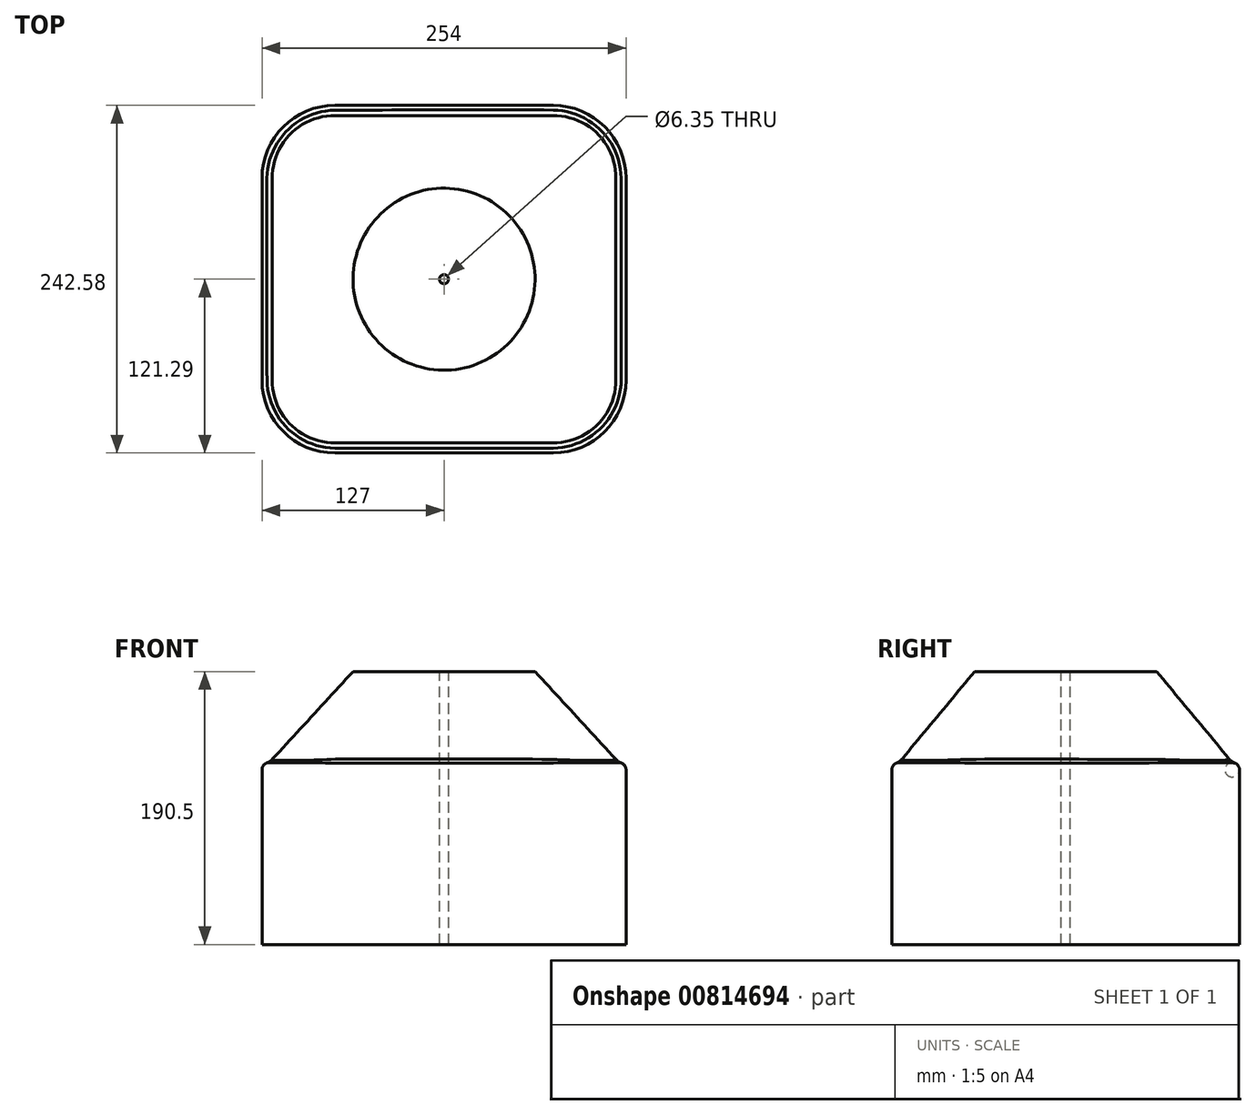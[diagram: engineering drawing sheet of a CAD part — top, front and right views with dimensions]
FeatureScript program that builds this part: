
annotation { "Feature Type Name" : "Feature", "Feature Type Description" : "" }
export const myFeature = defineFeature(function(context is Context, id is Id, definition is map)
    precondition{}
    {
        {
            var Q0;
            Q0=qCreatedBy(makeId("Front.planeOp"),FACE);
            var sketch = newSketch(context, id + "F0", { "sketchPlane" : qUnion([Q0])});
            skLineSegment(sketch, "E0.bottom", {"start": v(-127, 63.5) * mm, "end": v(127, 63.5) * mm});
            skLineSegment(sketch, "E0.top", {"start": v(-127, -63.5) * mm, "end": v(127, -63.5) * mm});
            skLineSegment(sketch, "E0.left", {"start": v(-127, 63.5) * mm, "end": v(-127, -63.5) * mm});
            skLineSegment(sketch, "E0.right", {"start": v(127, 63.5) * mm, "end": v(127, -63.5) * mm});
            skLineSegment(sketch, "E1", {"start": v(127, 63.5) * mm, "end": v(-127, -63.5) * mm, "construction": true});
            skSolve(sketch);
        }
        {
            var Q0;
            Q0 = qSketchRegion(id + "F0", true);
            extrude(context, id + "F1", {"entities" : qUnion([Q0]), "endBound" : BoundingType.SYMMETRIC, "oppositeDirection" : true, "depth" : 242.57 * mm, "offsetDistance" : 25.4 * mm});
        }
        {
            var Q0;
            Q0=makeQuery(id+"F1.opExtrude","SWEPT_EDGE",EDGE,{"disambiguationData":[OSD([sQuery(id+"F0.wireOp",EDGE,"E0.bottom"),sQuery(id+"F0.wireOp",EDGE,"E0.right")])]});
            var Q1;
            Q1=makeQuery(id+"F1.opExtrude","CAP_EDGE",EDGE,{"disambiguationData":[OSD([sQuery(id+"F0.wireOp",EDGE,"E0.bottom")])],"isStart":false});
            var Q2;
            Q2=makeQuery(id+"F1.opExtrude","SWEPT_EDGE",EDGE,{"disambiguationData":[OSD([sQuery(id+"F0.wireOp",EDGE,"E0.bottom"),sQuery(id+"F0.wireOp",EDGE,"E0.left")])]});
            var Q3;
            Q3=makeQuery(id+"F1.opExtrude","CAP_EDGE",EDGE,{"disambiguationData":[OSD([sQuery(id+"F0.wireOp",EDGE,"E0.bottom")])],"isStart":true});
            fillet(context, id + "F2", {"entities" : qUnion([Q0, Q1, Q2, Q3]), "radius" : 5.08 * mm, "tangentPropagation" : true, "allowEdgeOverflow" : false});
        }
        {
            var Q0;
            Q0=makeQuery(id+"F1.opExtrude","CAP_EDGE",EDGE,{"disambiguationData":[OSD([sQuery(id+"F0.wireOp",EDGE,"E0.right")])],"isStart":false});
            var Q1;
            Q1=makeQuery(id+"F1.opExtrude","CAP_EDGE",EDGE,{"disambiguationData":[OSD([sQuery(id+"F0.wireOp",EDGE,"E0.left")])],"isStart":false});
            var Q2;
            Q2=makeQuery(id+"F1.opExtrude","CAP_EDGE",EDGE,{"disambiguationData":[OSD([sQuery(id+"F0.wireOp",EDGE,"E0.right")])],"isStart":true});
            var Q3;
            Q3=makeQuery(id+"F1.opExtrude","CAP_EDGE",EDGE,{"disambiguationData":[OSD([sQuery(id+"F0.wireOp",EDGE,"E0.left")])],"isStart":true});
            fillet(context, id + "F3", {"entities" : qUnion([Q0, Q1, Q2, Q3]), "radius" : 50.8 * mm, "tangentPropagation" : true, "allowEdgeOverflow" : false});
        }
        {
            var Q0;
            Q0=makeQuery(id+"F1.opExtrude","SWEPT_FACE",FACE,{"disambiguationData":[OSD([sQuery(id+"F0.wireOp",EDGE,"E0.bottom")])]});
            var sketch = newSketch(context, id + "F4", { "sketchPlane" : qUnion([Q0])});
            skLineSegment(sketch, "E2.0", {"start": v(-121.92, 70.48) * mm, "end": v(-121.92, -70.48) * mm});
            skArc(sketch, "E3.0", {"start": v(-76.2, -116.2) * mm, "mid": v(-108.53, -102.81) * mm, "end": v(-121.92, -70.48) * mm});
            skLineSegment(sketch, "E3.1", {"start": v(-76.2, -116.2) * mm, "end": v(76.2, -116.2) * mm});
            skArc(sketch, "E3.2", {"start": v(121.92, -70.48) * mm, "mid": v(108.53, -102.81) * mm, "end": v(76.2, -116.2) * mm});
            skLineSegment(sketch, "E3.3", {"start": v(121.92, -70.48) * mm, "end": v(121.92, 70.48) * mm});
            skArc(sketch, "E3.4", {"start": v(76.2, 116.2) * mm, "mid": v(108.53, 102.81) * mm, "end": v(121.92, 70.48) * mm});
            skLineSegment(sketch, "E3.5", {"start": v(76.2, 116.2) * mm, "end": v(-76.2, 116.2) * mm});
            skArc(sketch, "E3.6", {"start": v(-121.92, 70.48) * mm, "mid": v(-108.53, 102.81) * mm, "end": v(-76.2, 116.2) * mm});
            skSolve(sketch);
        }
        {
            var Q0;
            Q0=qCreatedBy(makeId("Top.planeOp"),FACE);
            cPlane(context, id + "F5", {"entities" : qUnion([Q0]), "cplaneType" : CPlaneType.OFFSET, "offset" : 127 * mm, "width" : 152.4 * mm, "height" : 152.4 * mm});
        }
        {
            var Q0;
            Q0=qCreatedBy(id+"F5.planeOp",FACE);
            var sketch = newSketch(context, id + "F6", { "sketchPlane" : qUnion([Q0])});
            skCircle(sketch, "E4", {"center": v(0, 0) * mm, "radius": 63.5 * mm});
            skSolve(sketch);
        }
        {
            var Q1;
            Q1 = qSketchRegion(id + "F4", true);
            var Q2;
            Q2 = qSketchRegion(id + "F6", true);
            loft(context, id + "F7", {"operationType" : NewBodyOperationType.ADD, "sheetProfilesArray" : [{ "sheetProfileEntities" : qUnion([Q1]) }, { "sheetProfileEntities" : qUnion([Q2]) }]});
        }
        {
            var Q0;
            {var subQ0=sQuery(id+"F0.wireOp",EDGE,"E0.bottom");Q0=makeQuery(id+"F7.boolean.opBoolean","MERGE",EDGE,{"derivedFrom":[makeQuery(id+"F2.opFillet","BLEND_EDGE",EDGE,{"blendedFrom":[makeQuery(id+"F1.opExtrude","SWEPT_EDGE",EDGE,{"disambiguationData":[OSD([subQ0,sQuery(id+"F0.wireOp",EDGE,"E0.right")])]}),makeQuery(id+"F1.opExtrude","SWEPT_FACE",FACE,{"disambiguationData":[OSD([subQ0])]})],"blendedInto":[makeQuery(id+"F1.opExtrude","SWEPT_FACE",FACE,{"disambiguationData":[OSD([subQ0])]})]}),makeQuery(id+"F7.opLoft","MID_CAP_EDGE",EDGE,{"disambiguationData":[OSD([sQuery(id+"F4.wireOp",EDGE,"E3.2"),sQuery(id+"F4.wireOp",EDGE,"E3.3"),sQuery(id+"F4.wireOp",EDGE,"E3.4")])],"capPos":0.0})]});}
            fillet(context, id + "F8", {"entities" : qUnion([Q0]), "radius" : 10.16 * mm, "tangentPropagation" : true, "allowEdgeOverflow" : false});
        }
        {
            var Q0;
            Q0=makeQuery(id+"F7.opLoft","CAP_FACE",FACE,{"disambiguationData":[OSD([makeQuery(id+"F6.imprint","IMPRINT",FACE,{"disambiguationData":[TD([[makeQuery(id+"F6.imprint","IMPRINT",EDGE,{"derivedFrom":sQuery(id+"F6.wireOp",EDGE,"E4")}),1.0]])]})])],"isStart":true});
            var sketch = newSketch(context, id + "F9", { "sketchPlane" : qUnion([Q0])});
            skPoint(sketch, "E5", {"position": v(0, 0) * mm});
            skSolve(sketch);
        }
        {
            var Q0;
            Q0=sQuery(id+"F9.wireOp",VERTEX,"E5");
            var Q1;
            Q1=makeQuery(id+"F1.opExtrude","SWEPT_BODY",BODY,{"disambiguationData":[OSD([sQuery(id+"F0.wireOp",EDGE,"E0.bottom"),sQuery(id+"F0.wireOp",EDGE,"E0.top"),sQuery(id+"F0.wireOp",EDGE,"E0.left"),sQuery(id+"F0.wireOp",EDGE,"E0.right")])]});
            hole(context, id + "F10", {"style" : HoleStyle.SIMPLE, "endStyle" : HoleEndStyle.THROUGH, "holeDiameter" : 6.35 * mm, "majorDiameter" : 6.35 * mm, "isTappedThrough" : true, "tappedDepth" : 12.7 * mm, "tapClearance" : 3, "locations" : qUnion([Q0]), "scope" : qUnion([Q1])});
        }
    });
